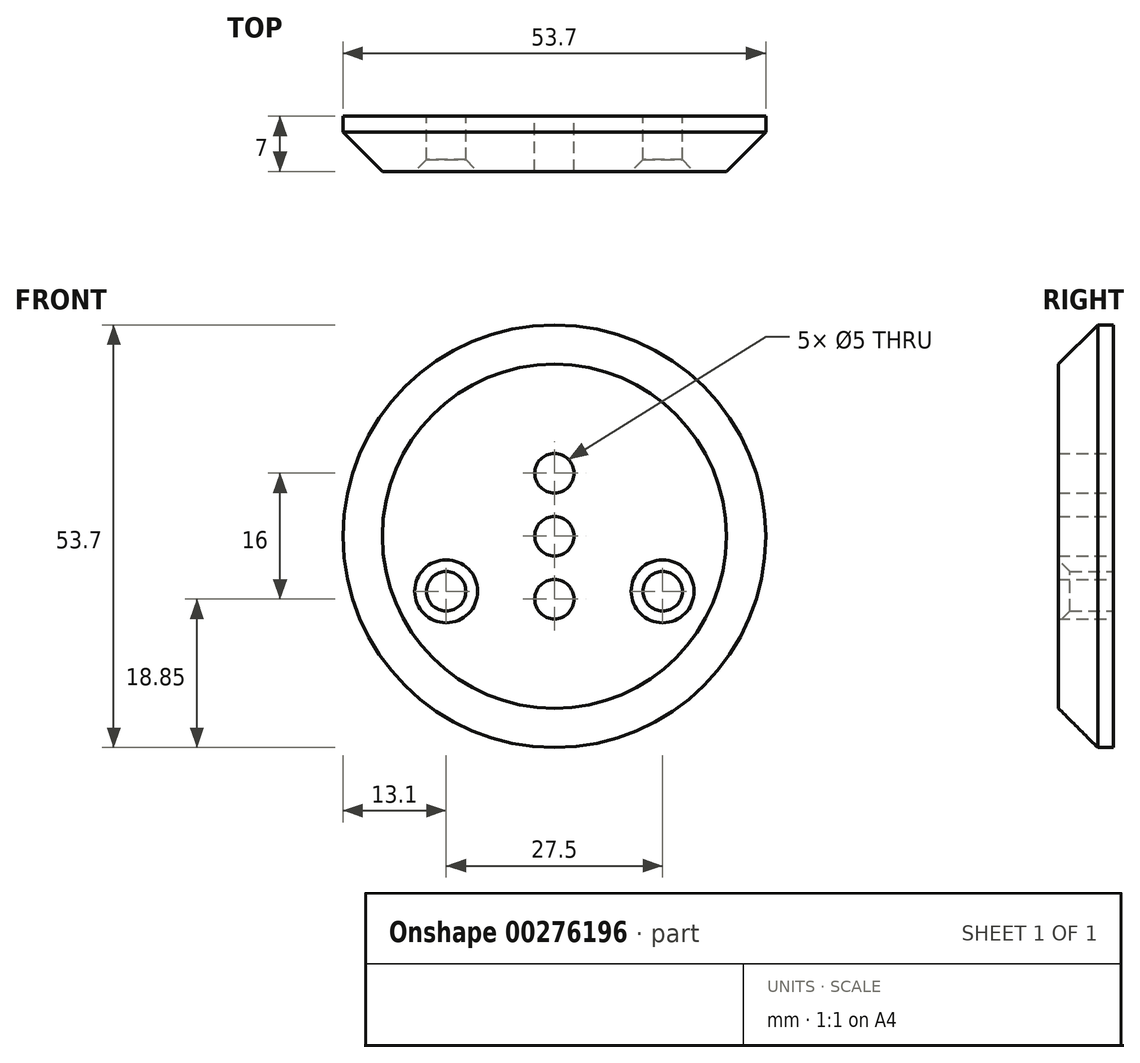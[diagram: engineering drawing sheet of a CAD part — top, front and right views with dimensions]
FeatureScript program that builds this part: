
annotation { "Feature Type Name" : "Feature", "Feature Type Description" : "" }
export const myFeature = defineFeature(function(context is Context, id is Id, definition is map)
    precondition{}
    {
        {
            var Q0;
            Q0=qCreatedBy(makeId("Front.planeOp"),FACE);
            var sketch = newSketch(context, id + "F0", { "sketchPlane" : qUnion([Q0])});
            skCircle(sketch, "E0", {"center": v(-13.75, 0) * mm, "radius": 2.5 * mm});
            skCircle(sketch, "E1.MirrorC", {"center": v(13.75, 0) * mm, "radius": 2.5 * mm});
            skCircle(sketch, "E2", {"center": v(0, 15) * mm, "radius": 2.5 * mm});
            skArc(sketch, "E3.0", {"start": v(-13.75, 5.5) * mm, "mid": v(-19.25, 0) * mm, "end": v(-13.75, -5.5) * mm, "construction": true});
            skArc(sketch, "E4.0", {"start": v(5.5, 15) * mm, "mid": v(0, 20.5) * mm, "end": v(-5.5, 15) * mm, "construction": true});
            skArc(sketch, "E5.0", {"start": v(13.75, 5.5) * mm, "mid": v(19.25, 0) * mm, "end": v(13.75, -5.5) * mm, "construction": true});
            skLineSegment(sketch, "E6", {"start": v(-13.75, -5.5) * mm, "end": v(13.75, -5.5) * mm, "construction": true});
            skLineSegment(sketch, "E7", {"start": v(5.5, 15) * mm, "end": v(5.5, 5.5) * mm, "construction": true});
            skLineSegment(sketch, "E8", {"start": v(-5.5, 15) * mm, "end": v(-5.5, 5.5) * mm, "construction": true});
            skLineSegment(sketch, "E9", {"start": v(-13.75, 5.5) * mm, "end": v(-5.5, 5.5) * mm, "construction": true});
            skLineSegment(sketch, "E10.trimOffspring", {"start": v(5.5, 5.5) * mm, "end": v(13.75, 5.5) * mm, "construction": true});
            skCircle(sketch, "E11", {"center": v(0, 7) * mm, "radius": 2.5 * mm});
            skCircle(sketch, "E12", {"center": v(0, -1) * mm, "radius": 2.5 * mm});
            skLineSegment(sketch, "E13", {"start": v(-17.8, 3.72) * mm, "end": v(-4.05, 18.72) * mm, "construction": true});
            skLineSegment(sketch, "E14", {"start": v(4.05, 18.72) * mm, "end": v(17.8, 3.72) * mm, "construction": true});
            skCircle(sketch, "E15", {"center": v(0, 7) * mm, "radius": 26.85 * mm});
            skSolve(sketch);
        }
        {
            var Q0;
            Q0=makeQuery(id+"F0.imprint","IMPRINT",FACE,{"disambiguationData":[TD([[makeQuery(id+"F0.imprint","IMPRINT",EDGE,{"derivedFrom":sQuery(id+"F0.wireOp",EDGE,"E0")}),-1.0]])]});
            extrude(context, id + "F1", {"entities" : qUnion([Q0]), "depth" : 7 * mm});
        }
        {
            var Q0;
            Q0=makeQuery(id+"F1.opExtrude","CAP_EDGE",EDGE,{"disambiguationData":[OSD([sQuery(id+"F0.wireOp",EDGE,"E0")])],"isStart":false});
            var Q1;
            Q1=makeQuery(id+"F1.opExtrude","CAP_EDGE",EDGE,{"disambiguationData":[OSD([sQuery(id+"F0.wireOp",EDGE,"E1.MirrorC")])],"isStart":false});
            chamfer(context, id + "F2", {"entities" : qUnion([Q0, Q1]), "width" : 1.5 * mm, "tangentPropagation" : true});
        }
        {
            var Q0;
            Q0=makeQuery(id+"F1.opExtrude","CAP_EDGE",EDGE,{"disambiguationData":[OSD([sQuery(id+"F0.wireOp",EDGE,"E15")])],"isStart":false});
            chamfer(context, id + "F3", {"entities" : qUnion([Q0]), "width" : 5 * mm, "tangentPropagation" : true});
        }
    });
